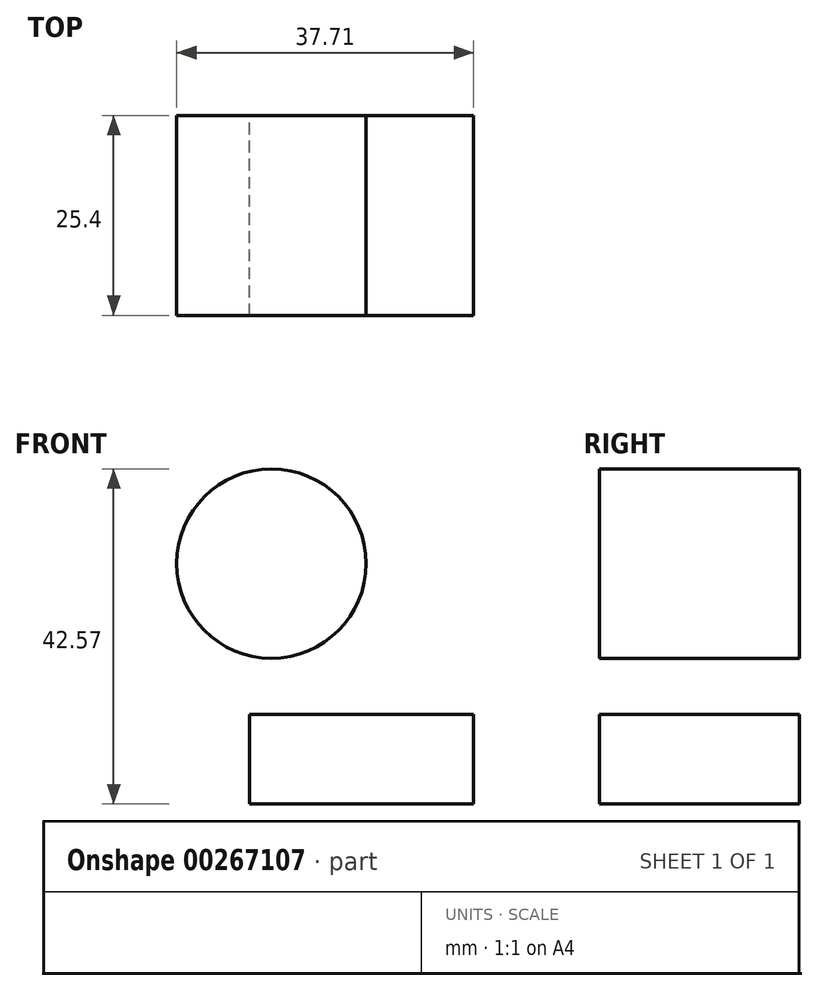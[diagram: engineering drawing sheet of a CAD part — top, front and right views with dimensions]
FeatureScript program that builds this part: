
annotation { "Feature Type Name" : "Feature", "Feature Type Description" : "" }
export const myFeature = defineFeature(function(context is Context, id is Id, definition is map)
    precondition{}
    {
        {
            var Q0;
            Q0=qCreatedBy(makeId("Front.planeOp"),FACE);
            var sketch = newSketch(context, id + "F0", { "sketchPlane" : qUnion([Q0])});
            skLineSegment(sketch, "E0.bottom", {"start": v(25.4, 25.4) * mm, "end": v(-25.4, 25.4) * mm});
            skLineSegment(sketch, "E0.top", {"start": v(25.4, -25.4) * mm, "end": v(-25.4, -25.4) * mm});
            skLineSegment(sketch, "E0.left", {"start": v(25.4, 25.4) * mm, "end": v(25.4, -25.4) * mm});
            skLineSegment(sketch, "E0.right", {"start": v(-25.4, 25.4) * mm, "end": v(-25.4, -25.4) * mm});
            skPoint(sketch, "E0.middle", {"position": v(0, 0) * mm});
            skCircle(sketch, "E1", {"center": v(-11.46, 12.3) * mm, "radius": 12.03 * mm});
            skPoint(sketch, "E1.first.point", {"position": v(-20.68, 20.03) * mm});
            skPoint(sketch, "E1.second.point", {"position": v(0, 8.66) * mm});
            skPoint(sketch, "E1.third.point", {"position": v(-20.16, 4) * mm});
            skLineSegment(sketch, "E2.bottom", {"start": v(14.22, -18.23) * mm, "end": v(-14.22, -18.23) * mm});
            skLineSegment(sketch, "E2.top", {"start": v(14.22, -6.85) * mm, "end": v(-14.22, -6.85) * mm});
            skLineSegment(sketch, "E2.left", {"start": v(14.22, -18.23) * mm, "end": v(14.22, -6.85) * mm});
            skLineSegment(sketch, "E2.right", {"start": v(-14.22, -18.23) * mm, "end": v(-14.22, -6.85) * mm});
            skPoint(sketch, "E2.middle", {"position": v(0, -12.54) * mm});
            skSolve(sketch);
        }
        {
            var Q0;
            Q0=makeQuery(id+"F0.imprint","IMPRINT",FACE,{"disambiguationData":[TD([[makeQuery(id+"F0.imprint","IMPRINT",EDGE,{"derivedFrom":sQuery(id+"F0.wireOp",EDGE,"E1")}),1.0]])]});
            var Q1;
            Q1=makeQuery(id+"F0.imprint","IMPRINT",FACE,{"disambiguationData":[TD([[makeQuery(id+"F0.imprint","IMPRINT",EDGE,{"derivedFrom":sQuery(id+"F0.wireOp",EDGE,"E2.bottom")}),-1.0]])]});
            extrude(context, id + "F1", {"entities" : qUnion([Q0, Q1]), "depth" : 25.4 * mm});
        }
    });
